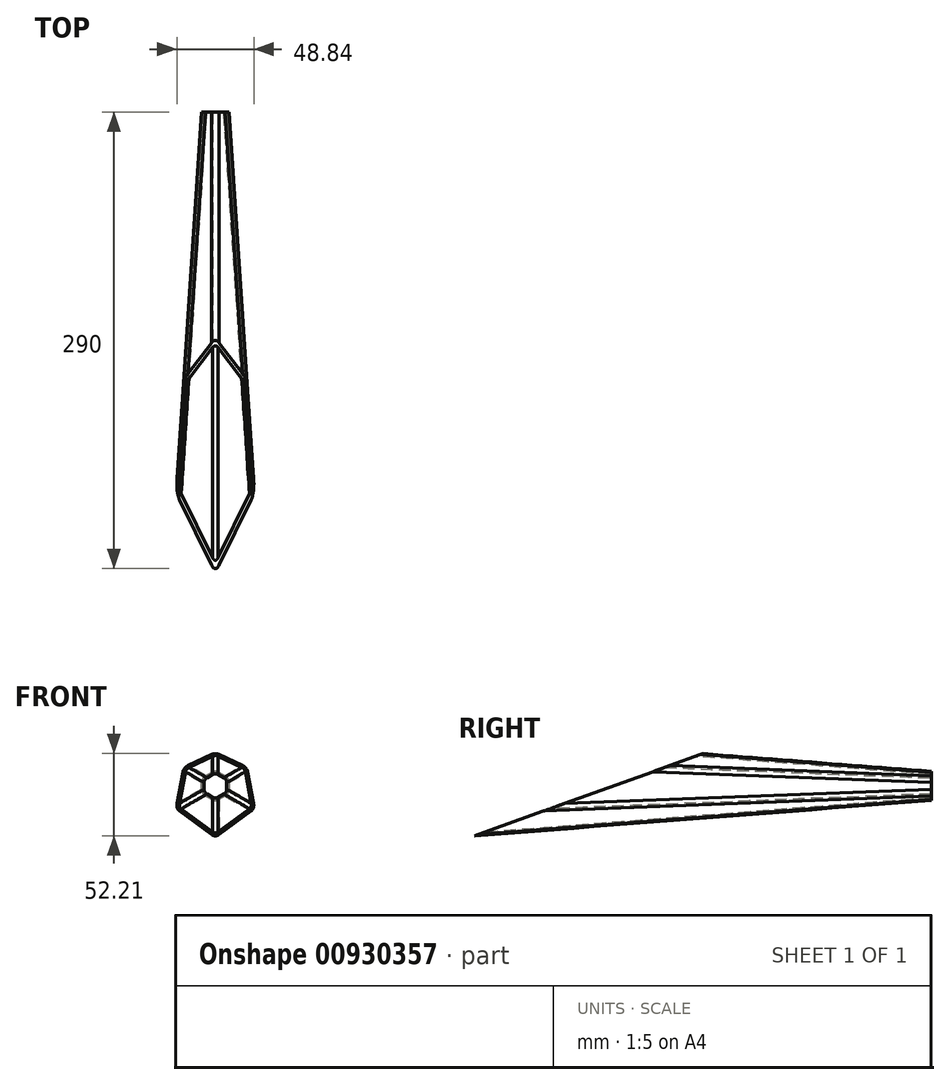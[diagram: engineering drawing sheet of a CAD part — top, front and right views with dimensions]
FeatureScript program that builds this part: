
annotation { "Feature Type Name" : "Feature", "Feature Type Description" : "" }
export const myFeature = defineFeature(function(context is Context, id is Id, definition is map)
    precondition{}
    {
        {
            var Q0;
            Q0=qCreatedBy(makeId("Right.planeOp"),FACE);
            var sketch = newSketch(context, id + "F0", { "sketchPlane" : qUnion([Q0])});
            skLineSegment(sketch, "E0", {"start": v(0, 134.22) * mm, "end": v(0, 0) * mm, "construction": true});
            skLineSegment(sketch, "E1", {"start": v(145, 0) * mm, "end": v(-145, 0) * mm, "construction": true});
            skLineSegment(sketch, "E2", {"start": v(145, 10) * mm, "end": v(145, -10) * mm});
            skLineSegment(sketch, "E3", {"start": v(-145, 32.5) * mm, "end": v(-145, -32.5) * mm});
            skLineSegment(sketch, "E4", {"start": v(145, 10) * mm, "end": v(-145, 32.5) * mm});
            skLineSegment(sketch, "E5", {"start": v(145, -10) * mm, "end": v(-145, -32.5) * mm});
            skLineSegment(sketch, "E6", {"start": v(-145, -32.5) * mm, "end": v(0, 21.25) * mm});
            skLineSegment(sketch, "E7", {"start": v(145, -10) * mm, "end": v(125.06, 11.55) * mm});
            skSolve(sketch);
        }
        {
            var Q0;
            Q0=sQuery(id+"F0.wireOp",EDGE,"E2");
            cPoint(context, id + "F1", {"entities" : qUnion([Q0]), "parameter" : 0.5});
        }
        {
            var Q0;
            Q0=qCreatedBy(makeId("Front.planeOp"),FACE);
            var Q1;
            Q1 = qCreatedBy(id + "F1" ,VERTEX);
            cPlane(context, id + "F2", {"entities" : qUnion([Q0, Q1]), "cplaneType" : CPlaneType.PLANE_POINT, "offset" : 25 * mm, "width" : 150 * mm, "height" : 150 * mm});
        }
        {
            var Q0;
            Q0=qCreatedBy(makeId("Front.planeOp"),FACE);
            var Q1;
            Q1=sQuery(id+"F0.wireOp",VERTEX,"E1.end");
            cPlane(context, id + "F3", {"entities" : qUnion([Q0, Q1]), "cplaneType" : CPlaneType.PLANE_POINT, "offset" : 25 * mm, "width" : 150 * mm, "height" : 150 * mm});
        }
        {
            var Q0;
            Q0=qCreatedBy(id+"F2.planeOp",FACE);
            var sketch = newSketch(context, id + "F4", { "sketchPlane" : qUnion([Q0])});
            skCircle(sketch, "E8.cCircle", {"center": v(0, 0) * mm, "radius": 8.66 * mm, "construction": true});
            skLineSegment(sketch, "E8.0", {"start": v(-8.66, 5) * mm, "end": v(0, 10) * mm});
            skLineSegment(sketch, "E8.1", {"start": v(0, 10) * mm, "end": v(8.66, 5) * mm});
            skLineSegment(sketch, "E8.2", {"start": v(8.66, 5) * mm, "end": v(8.66, -5) * mm});
            skLineSegment(sketch, "E8.3", {"start": v(8.66, -5) * mm, "end": v(0, -10) * mm});
            skLineSegment(sketch, "E8.4", {"start": v(0, -10) * mm, "end": v(-8.66, -5) * mm});
            skLineSegment(sketch, "E8.5", {"start": v(-8.66, -5) * mm, "end": v(-8.66, 5) * mm});
            skPoint(sketch, "E8.0.midPoint", {"position": v(-4.33, 7.5) * mm});
            skLineSegment(sketch, "E9", {"start": v(0, 32.22) * mm, "end": v(0, 0) * mm, "construction": true});
            skLineSegment(sketch, "E10", {"start": v(0, 0) * mm, "end": v(-23.52, 0) * mm, "construction": true});
            skPoint(sketch, "E10.endSnap0", {"position": v(8.66, 0) * mm});
            skPoint(sketch, "E11.0", {"position": v(0, 10) * mm});
            skSolve(sketch);
        }
        {
            var Q0;
            Q0=qCreatedBy(id+"F3.planeOp",FACE);
            var sketch = newSketch(context, id + "F5", { "sketchPlane" : qUnion([Q0])});
            skLineSegment(sketch, "E12", {"start": v(0, 32.5) * mm, "end": v(0, 0) * mm});
            skLineSegment(sketch, "E13", {"start": v(0, 0) * mm, "end": v(28.15, 0) * mm, "construction": true});
            skCircle(sketch, "E14.cCircle", {"center": v(0, 0) * mm, "radius": 28.15 * mm, "construction": true});
            skLineSegment(sketch, "E14.0", {"start": v(0, 32.5) * mm, "end": v(28.15, 16.25) * mm});
            skLineSegment(sketch, "E14.1", {"start": v(28.15, 16.25) * mm, "end": v(28.15, -16.25) * mm});
            skLineSegment(sketch, "E14.2", {"start": v(28.15, -16.25) * mm, "end": v(0, -32.5) * mm});
            skLineSegment(sketch, "E14.3", {"start": v(0, -32.5) * mm, "end": v(-28.15, -16.25) * mm});
            skLineSegment(sketch, "E14.4", {"start": v(-28.15, -16.25) * mm, "end": v(-28.15, 16.25) * mm});
            skLineSegment(sketch, "E14.5", {"start": v(-28.15, 16.25) * mm, "end": v(0, 32.5) * mm});
            skPoint(sketch, "E14.0.midPoint", {"position": v(14.07, 24.37) * mm});
            skPoint(sketch, "E15.0", {"position": v(0, 32.5) * mm});
            skSolve(sketch);
        }
        {
            var Q0;
            Q0=qCreatedBy(id+"F3.planeOp",FACE);
            var sketch = newSketch(context, id + "F6", { "sketchPlane" : qUnion([Q0])});
            skCircle(sketch, "E16.cCircle", {"center": v(0, 0) * mm, "radius": 28.15 * mm, "construction": true});
            skLineSegment(sketch, "E16.0", {"start": v(2.5, 31.06) * mm, "end": v(25.65, 17.7) * mm});
            skLineSegment(sketch, "E16.1", {"start": v(28.15, 13.36) * mm, "end": v(28.15, -13.36) * mm});
            skLineSegment(sketch, "E16.2", {"start": v(25.65, -17.7) * mm, "end": v(2.5, -31.06) * mm});
            skLineSegment(sketch, "E16.3", {"start": v(-2.5, -31.06) * mm, "end": v(-25.65, -17.7) * mm});
            skLineSegment(sketch, "E16.4", {"start": v(-28.15, -13.36) * mm, "end": v(-28.15, 13.36) * mm});
            skLineSegment(sketch, "E16.5", {"start": v(-25.65, 17.7) * mm, "end": v(-2.5, 31.06) * mm});
            skPoint(sketch, "E16.0.midPoint", {"position": v(14.07, 24.37) * mm});
            skPoint(sketch, "E17.visualSharp", {"position": v(0, 32.5) * mm});
            skArc(sketch, "E17.filletArc", {"start": v(2.5, 31.06) * mm, "mid": v(0, 31.73) * mm, "end": v(-2.5, 31.06) * mm});
            skPoint(sketch, "E18.visualSharp", {"position": v(-28.15, 16.25) * mm});
            skArc(sketch, "E18.filletArc", {"start": v(-25.65, 17.7) * mm, "mid": v(-27.48, 15.86) * mm, "end": v(-28.15, 13.36) * mm});
            skPoint(sketch, "E19.visualSharp", {"position": v(28.15, 16.25) * mm});
            skArc(sketch, "E19.filletArc", {"start": v(28.15, 13.36) * mm, "mid": v(27.48, 15.86) * mm, "end": v(25.65, 17.7) * mm});
            skPoint(sketch, "E20.visualSharp", {"position": v(28.15, -16.25) * mm});
            skArc(sketch, "E20.filletArc", {"start": v(25.65, -17.7) * mm, "mid": v(27.48, -15.86) * mm, "end": v(28.15, -13.36) * mm});
            skPoint(sketch, "E21.visualSharp", {"position": v(-28.15, -16.25) * mm});
            skArc(sketch, "E21.filletArc", {"start": v(-28.15, -13.36) * mm, "mid": v(-27.48, -15.86) * mm, "end": v(-25.65, -17.7) * mm});
            skPoint(sketch, "E22.visualSharp", {"position": v(0, -32.5) * mm});
            skArc(sketch, "E22.filletArc", {"start": v(-2.5, -31.06) * mm, "mid": v(0, -31.73) * mm, "end": v(2.5, -31.06) * mm});
            skSolve(sketch);
        }
        {
            var Q0;
            Q0=qCreatedBy(id+"F2.planeOp",FACE);
            var sketch = newSketch(context, id + "F7", { "sketchPlane" : qUnion([Q0])});
            skCircle(sketch, "E23.cCircle", {"center": v(0, 0) * mm, "radius": 8.66 * mm, "construction": true});
            skLineSegment(sketch, "E23.0", {"start": v(2.5, 8.56) * mm, "end": v(6.16, 6.44) * mm});
            skLineSegment(sketch, "E23.1", {"start": v(8.66, 2.11) * mm, "end": v(8.66, -2.11) * mm});
            skLineSegment(sketch, "E23.2", {"start": v(6.16, -6.44) * mm, "end": v(2.5, -8.56) * mm});
            skLineSegment(sketch, "E23.3", {"start": v(-2.5, -8.56) * mm, "end": v(-6.16, -6.44) * mm});
            skLineSegment(sketch, "E23.4", {"start": v(-8.66, -2.11) * mm, "end": v(-8.66, 2.11) * mm});
            skLineSegment(sketch, "E23.5", {"start": v(-6.16, 6.44) * mm, "end": v(-2.5, 8.56) * mm});
            skPoint(sketch, "E23.0.midPoint", {"position": v(4.33, 7.5) * mm});
            skPoint(sketch, "E24.visualSharp", {"position": v(0, 10) * mm});
            skArc(sketch, "E24.filletArc", {"start": v(2.5, 8.56) * mm, "mid": v(0, 9.23) * mm, "end": v(-2.5, 8.56) * mm});
            skPoint(sketch, "E25.visualSharp", {"position": v(8.66, 5) * mm});
            skArc(sketch, "E25.filletArc", {"start": v(8.66, 2.11) * mm, "mid": v(8, 4.61) * mm, "end": v(6.16, 6.44) * mm});
            skPoint(sketch, "E26.visualSharp", {"position": v(8.66, -5) * mm});
            skArc(sketch, "E26.filletArc", {"start": v(6.16, -6.44) * mm, "mid": v(8, -4.61) * mm, "end": v(8.66, -2.11) * mm});
            skPoint(sketch, "E27.visualSharp", {"position": v(0, -10) * mm});
            skArc(sketch, "E27.filletArc", {"start": v(-2.5, -8.56) * mm, "mid": v(0, -9.23) * mm, "end": v(2.5, -8.56) * mm});
            skPoint(sketch, "E28.visualSharp", {"position": v(-8.66, -5) * mm});
            skArc(sketch, "E28.filletArc", {"start": v(-8.66, -2.11) * mm, "mid": v(-8, -4.61) * mm, "end": v(-6.16, -6.44) * mm});
            skPoint(sketch, "E29.visualSharp", {"position": v(-8.66, 5) * mm});
            skArc(sketch, "E29.filletArc", {"start": v(-6.16, 6.44) * mm, "mid": v(-8, 4.61) * mm, "end": v(-8.66, 2.11) * mm});
            skSolve(sketch);
        }
        {
            var Q0;
            Q0=qCreatedBy(makeId("Right.planeOp"),FACE);
            var sketch = newSketch(context, id + "F8", { "sketchPlane" : qUnion([Q0])});
            skLineSegment(sketch, "E30", {"start": v(-145, 31.73) * mm, "end": v(145, 9.23) * mm});
            skLineSegment(sketch, "E31", {"start": v(145, -9.23) * mm, "end": v(-145, -31.73) * mm});
            skPoint(sketch, "E32.0", {"position": v(-145, 31.73) * mm});
            skPoint(sketch, "E33.0", {"position": v(-145, -31.73) * mm});
            skPoint(sketch, "E34.0", {"position": v(145, 9.23) * mm});
            skPoint(sketch, "E35.0", {"position": v(145, -9.23) * mm});
            skSolve(sketch);
        }
        {
            var Q0;
            Q0=sQuery(id+"F8.wireOp",EDGE,"E30");
            var Q1;
            Q1 = qSketchRegion(id + "F7", true);
            var Q2;
            Q2 = qSketchRegion(id + "F6", true);
            loft(context, id + "F9", {"addSections" : true, "spine" : qUnion([Q0]), "sectionCount" : 5, "sheetProfilesArray" : [{ "sheetProfileEntities" : qUnion([Q1]) }, { "sheetProfileEntities" : qUnion([Q2]) }]});
        }
        {
            var Q0;
            Q0=makeQuery(id+"F9.opLoft","CAP_FACE",FACE,{"disambiguationData":[OSD([makeQuery(id+"F6.imprint","IMPRINT",FACE,{"disambiguationData":[TD([[makeQuery(id+"F6.imprint","IMPRINT",EDGE,{"derivedFrom":sQuery(id+"F6.wireOp",EDGE,"E16.0")}),-1.0]])]})])],"isStart":true});
            var Q1;
            Q1=makeQuery(id+"F9.opLoft","CAP_FACE",FACE,{"disambiguationData":[OSD([makeQuery(id+"F7.imprint","IMPRINT",FACE,{"disambiguationData":[TD([[makeQuery(id+"F7.imprint","IMPRINT",EDGE,{"derivedFrom":sQuery(id+"F7.wireOp",EDGE,"E23.0")}),-1.0]])]})])],"isStart":true});
            shell(context, id + "F10", {"entities" : qUnion([Q0, Q1]), "thickness" : 1.5 * mm});
        }
        {
            var Q0;
            Q0=qCreatedBy(makeId("Right.planeOp"),FACE);
            var sketch = newSketch(context, id + "F11", { "sketchPlane" : qUnion([Q0])});
            skLineSegment(sketch, "E36.0", {"start": v(-145, 31.73) * mm, "end": v(145, 9.23) * mm, "construction": true});
            skLineSegment(sketch, "E37.0", {"start": v(145, -9.23) * mm, "end": v(-145, -31.73) * mm, "construction": true});
            skLineSegment(sketch, "E38", {"start": v(-145, 31.73) * mm, "end": v(-145, -31.73) * mm});
            skLineSegment(sketch, "E39", {"start": v(0, 31.73) * mm, "end": v(0, 0) * mm, "construction": true});
            skLineSegment(sketch, "E40", {"start": v(0, 0) * mm, "end": v(-145, 0) * mm, "construction": true});
            skLineSegment(sketch, "E41", {"start": v(-145, -31.73) * mm, "end": v(0, 20.48) * mm});
            skLineSegment(sketch, "E42", {"start": v(0, 20.48) * mm, "end": v(-145, 31.73) * mm});
            skLineSegment(sketch, "E43.0", {"start": v(-150, 37.13) * mm, "end": v(-150, -33.53) * mm});
            skLineSegment(sketch, "E44.0", {"start": v(-150, 37.13) * mm, "end": v(145.39, 14.21) * mm});
            skLineSegment(sketch, "E45", {"start": v(0, 20.48) * mm, "end": v(0, 25.5) * mm});
            skLineSegment(sketch, "E46", {"start": v(-145, -31.73) * mm, "end": v(-150, -33.53) * mm});
            skSolve(sketch);
        }
        {
            var Q0;
            Q0 = qSketchRegion(id + "F11", true);
            extrude(context, id + "F12", {"entities" : qUnion([Q0]), "operationType" : NewBodyOperationType.REMOVE, "endBound" : BoundingType.THROUGH_ALL, "oppositeDirection" : true, "depth" : 25 * mm, "offsetDistance" : 25 * mm, "hasSecondDirection" : true, "secondDirectionBound" : SecondDirectionBoundingType.THROUGH_ALL, "secondDirectionOppositeDirection" : false, "secondDirectionDepth" : 25 * mm});
        }
    });
